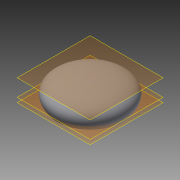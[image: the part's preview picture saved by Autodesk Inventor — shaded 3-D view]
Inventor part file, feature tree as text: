
AUTODESK INVENTOR PART (.ipt)
format: ipt  version: 2014 (Build 180170000, 170)  size: 148,480 bytes
history: native  units: mm
features: plane x3, sketch x3, loft x1
ambient origin geometry x8: Origin, YZ Plane, XZ Plane, XY Plane, X Axis, Y Axis, Z Axis, Center Point
bodies: Solid1 (feature_tree)
feature tree (7):
  plane  "Work Plane1"
  sketch  "Sketch2"  dims[d0=20.0mm d1=150.0mm]
  plane  "Work Plane2"
  sketch  "Sketch3"  dims[d2=0.0mm d3=90.0deg]
  plane  "Work Plane3"
  loft  "Loft1"
  sketch  "Sketch4"  dims[d4=0.0mm d5=90.0deg d6=0.0mm d7=90.0deg]
